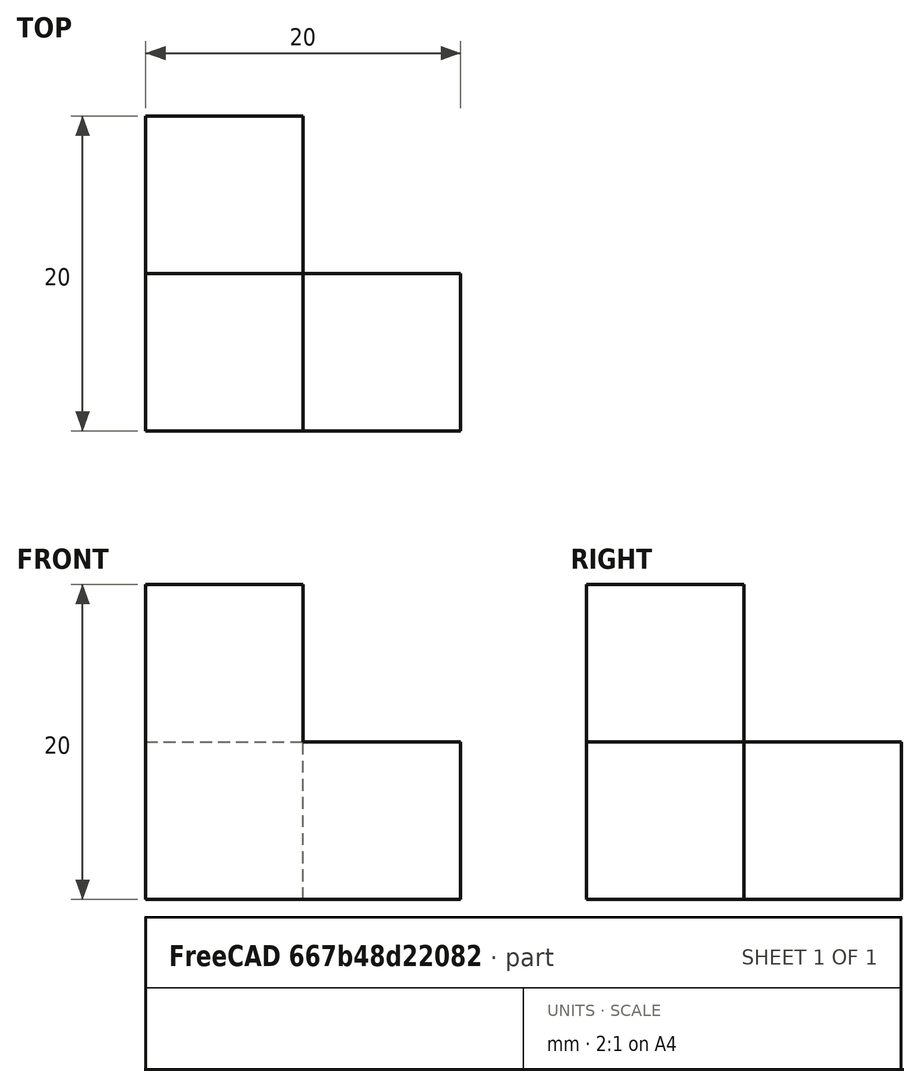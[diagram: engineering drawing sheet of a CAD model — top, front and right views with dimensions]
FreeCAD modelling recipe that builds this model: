
FCSTD DOCUMENT  (FreeCAD 0.21R33694 (Git))
Label: OJT1_T05P04_qubert2-fusion
License: All rights reserved
LicenseURL: http://en.wikipedia.org/wiki/All_rights_reserved
objects: Part::Box×4, Part::MultiFuse×1
note: 5 computed .brp shape members not serialized (recipe doc carries the construction recipe); baked Part::Feature solids carry a one-line shape summary decoded from their .brp

FEATURE [Part::Box] Box  label="cubo1"
  AttacherType = Attacher::AttachEngine3D
  Height = 10
  Length = 10
  Placement = pos=(0,10,0) rot=(0,0,1;0rad)
  Width = 10
FEATURE [Part::Box] Box001  label="cubo2"
  AttacherType = Attacher::AttachEngine3D
  Height = 10
  Length = 10
  Width = 10
FEATURE [Part::Box] Box002  label="cubo3"
  AttacherType = Attacher::AttachEngine3D
  Height = 10
  Length = 10
  Placement = pos=(10,0,0) rot=(0,0,1;0rad)
  Width = 10
FEATURE [Part::Box] Box003  label="cubo4"
  AttacherType = Attacher::AttachEngine3D
  Height = 20
  Length = 10
  Width = 10
FEATURE [Part::MultiFuse] Fusion  label="qubert2_fusion"
  Refine = true
  Shapes = -> [Box,Box001,Box002,Box003]
